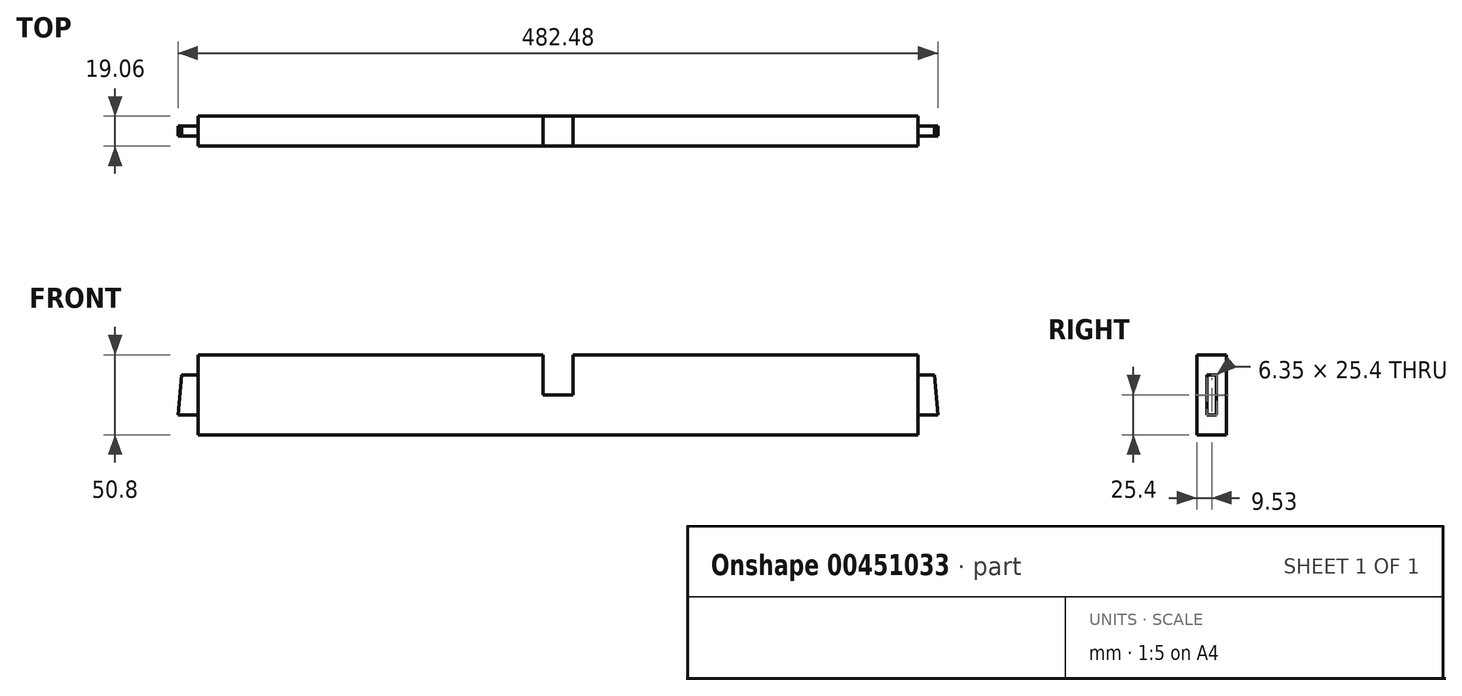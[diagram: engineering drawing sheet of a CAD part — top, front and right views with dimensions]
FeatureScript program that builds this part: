
annotation { "Feature Type Name" : "Feature", "Feature Type Description" : "" }
export const myFeature = defineFeature(function(context is Context, id is Id, definition is map)
    precondition{}
    {
        {
            var Q0;
            Q0=qCreatedBy(makeId("Front.planeOp"),FACE);
            var sketch = newSketch(context, id + "F0", { "sketchPlane" : qUnion([Q0])});
            skLineSegment(sketch, "E0.bottom", {"start": v(-228.6, 25.4) * mm, "end": v(228.6, 25.4) * mm});
            skLineSegment(sketch, "E0.top", {"start": v(-228.6, -25.4) * mm, "end": v(228.6, -25.4) * mm});
            skLineSegment(sketch, "E0.left", {"start": v(-228.6, 25.4) * mm, "end": v(-228.6, -25.4) * mm});
            skLineSegment(sketch, "E0.right", {"start": v(228.6, 25.4) * mm, "end": v(228.6, -25.4) * mm});
            skPoint(sketch, "E0.middle", {"position": v(0, 0) * mm});
            skSolve(sketch);
        }
        {
            var Q0;
            Q0=makeQuery(id+"F0.imprint","IMPRINT",FACE,{"disambiguationData":[TD([[makeQuery(id+"F0.imprint","IMPRINT",EDGE,{"derivedFrom":sQuery(id+"F0.wireOp",EDGE,"E0.bottom")}),-1.0]])]});
            extrude(context, id + "F1", {"entities" : qUnion([Q0]), "endBound" : BoundingType.SYMMETRIC, "depth" : 19.05 * mm});
        }
        {
            var Q0;
            Q0=makeQuery(id+"F1.opExtrude","SWEPT_FACE",FACE,{"disambiguationData":[OSD([sQuery(id+"F0.wireOp",EDGE,"E0.bottom")])]});
            var sketch = newSketch(context, id + "F2", { "sketchPlane" : qUnion([Q0])});
            skLineSegment(sketch, "E1", {"start": v(-9.52, 9.53) * mm, "end": v(9.52, 9.53) * mm});
            skLineSegment(sketch, "E2", {"start": v(9.52, -9.53) * mm, "end": v(9.52, 9.53) * mm});
            skLineSegment(sketch, "E3", {"start": v(-9.52, 9.53) * mm, "end": v(-9.52, -9.53) * mm});
            skLineSegment(sketch, "E4", {"start": v(-9.52, -9.53) * mm, "end": v(9.52, -9.53) * mm});
            skSolve(sketch);
        }
        {
            var Q0;
            Q0=makeQuery(id+"F2.imprint","IMPRINT",FACE,{"disambiguationData":[TD([[makeQuery(id+"F2.imprint","IMPRINT",EDGE,{"derivedFrom":sQuery(id+"F2.wireOp",EDGE,"E1")}),-1.0]])]});
            extrude(context, id + "F3", {"entities" : qUnion([Q0]), "operationType" : NewBodyOperationType.REMOVE, "endBound" : BoundingType.SYMMETRIC, "oppositeDirection" : true, "depth" : 50.8 * mm});
        }
        {
            var Q0;
            Q0=makeQuery(id+"F1.opExtrude","SWEPT_FACE",FACE,{"disambiguationData":[OSD([sQuery(id+"F0.wireOp",EDGE,"E0.left")])]});
            var sketch = newSketch(context, id + "F4", { "sketchPlane" : qUnion([Q0])});
            skLineSegment(sketch, "E5.bottom", {"start": v(-3.18, 12.7) * mm, "end": v(3.18, 12.7) * mm});
            skLineSegment(sketch, "E5.top", {"start": v(-3.18, -12.7) * mm, "end": v(3.17, -12.7) * mm});
            skLineSegment(sketch, "E5.left", {"start": v(-3.18, 12.7) * mm, "end": v(-3.18, -12.7) * mm});
            skLineSegment(sketch, "E5.right", {"start": v(3.18, 12.7) * mm, "end": v(3.17, -12.7) * mm});
            skPoint(sketch, "E5.middle", {"position": v(0, 0) * mm});
            skSolve(sketch);
        }
        {
            var Q0;
            Q0=makeQuery(id+"F4.imprint","IMPRINT",FACE,{"disambiguationData":[TD([[makeQuery(id+"F4.imprint","IMPRINT",EDGE,{"derivedFrom":sQuery(id+"F4.wireOp",EDGE,"E5.bottom")}),-1.0]])]});
            var Q1;
            Q1 = qSketchRegion(id + "F6", true);
            extrude(context, id + "F5", {"entities" : qUnion([Q0, Q1]), "operationType" : NewBodyOperationType.ADD, "endBound" : BoundingType.SYMMETRIC, "depth" : 25.4 * mm});
        }
        {
            var Q0;
            Q0=makeQuery(id+"F1.opExtrude","SWEPT_FACE",FACE,{"disambiguationData":[OSD([sQuery(id+"F0.wireOp",EDGE,"E0.right")])]});
            var sketch = newSketch(context, id + "F6", { "sketchPlane" : qUnion([Q0])});
            skLineSegment(sketch, "E6.bottom", {"start": v(-3.18, 12.7) * mm, "end": v(3.17, 12.7) * mm});
            skLineSegment(sketch, "E6.top", {"start": v(-3.18, -12.7) * mm, "end": v(3.17, -12.7) * mm});
            skLineSegment(sketch, "E6.left", {"start": v(-3.18, 12.7) * mm, "end": v(-3.18, -12.7) * mm});
            skLineSegment(sketch, "E6.right", {"start": v(3.17, 12.7) * mm, "end": v(3.17, -12.7) * mm});
            skPoint(sketch, "E6.middle", {"position": v(0, 0) * mm});
            skSolve(sketch);
        }
        {
            var Q0;
            Q0=makeQuery(id+"F6.imprint","IMPRINT",FACE,{"disambiguationData":[TD([[makeQuery(id+"F6.imprint","IMPRINT",EDGE,{"derivedFrom":sQuery(id+"F6.wireOp",EDGE,"E6.bottom")}),-1.0]])]});
            extrude(context, id + "F7", {"entities" : qUnion([Q0]), "operationType" : NewBodyOperationType.ADD, "endBound" : BoundingType.SYMMETRIC, "depth" : 25.4 * mm});
        }
        {
            var Q0;
            Q0=makeQuery(id+"F7.opExtrude","CAP_EDGE",EDGE,{"disambiguationData":[OSD([sQuery(id+"F6.wireOp",EDGE,"E6.bottom")])],"isStart":false});
            var Q1;
            Q1=makeQuery(id+"F5.opExtrude","CAP_EDGE",EDGE,{"disambiguationData":[OSD([sQuery(id+"F4.wireOp",EDGE,"E5.bottom")])],"isStart":false});
            chamfer(context, id + "F8", {"entities" : qUnion([Q0, Q1]), "chamferType" : ChamferType.OFFSET_ANGLE, "width" : 2.3 * mm, "oppositeDirection" : false, "angle" : 85 * degree, "tangentPropagation" : true});
        }
    });
